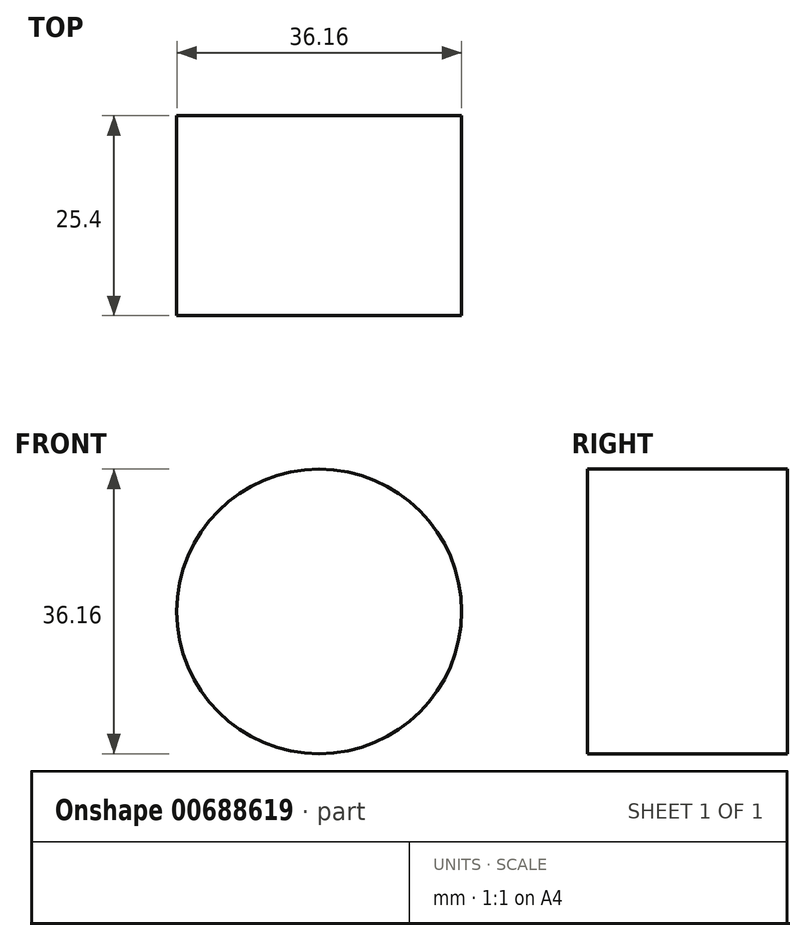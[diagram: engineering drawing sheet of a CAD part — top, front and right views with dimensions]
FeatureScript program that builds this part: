
annotation { "Feature Type Name" : "Feature", "Feature Type Description" : "" }
export const myFeature = defineFeature(function(context is Context, id is Id, definition is map)
    precondition{}
    {
        {
            var Q0;
            Q0=qCreatedBy(makeId("Front.planeOp"),FACE);
            var sketch = newSketch(context, id + "F0", { "sketchPlane" : qUnion([Q0])});
            skCircle(sketch, "E0", {"center": v(0, 0) * mm, "radius": 18.08 * mm});
            skSolve(sketch);
        }
        {
            var Q0;
            Q0 = qSketchRegion(id + "F0", true);
            extrude(context, id + "F1", {"entities" : qUnion([Q0]), "depth" : 25.4 * mm, "offsetDistance" : 25.4 * mm});
        }
    });
